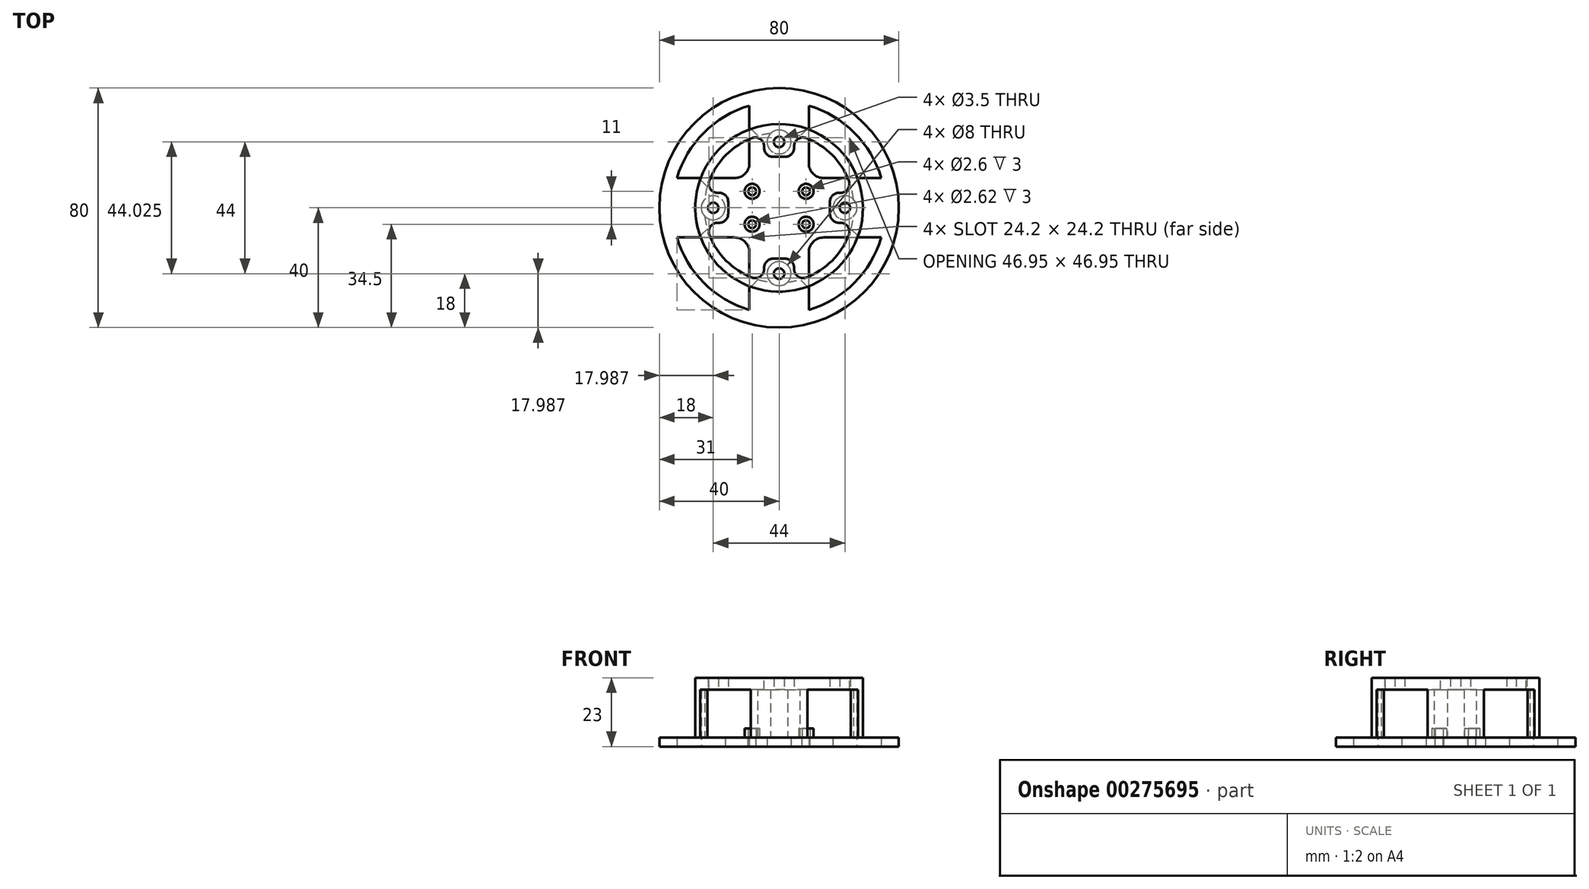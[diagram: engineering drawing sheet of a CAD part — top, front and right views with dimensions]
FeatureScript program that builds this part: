
annotation { "Feature Type Name" : "Feature", "Feature Type Description" : "" }
export const myFeature = defineFeature(function(context is Context, id is Id, definition is map)
    precondition{}
    {
        {
            var Q0;
            Q0=qCreatedBy(makeId("Top.planeOp"),FACE);
            var sketch = newSketch(context, id + "F0", { "sketchPlane" : qUnion([Q0])});
            skCircle(sketch, "E0", {"center": v(0, 0) * mm, "radius": 40 * mm});
            skSolve(sketch);
        }
        {
            var Q0;
            Q0 = qSketchRegion(id + "F0", true);
            extrude(context, id + "F1", {"entities" : qUnion([Q0]), "depth" : 3 * mm});
        }
        {
            var Q0;
            Q0=makeQuery(id+"F1.opExtrude","CAP_FACE",FACE,{"disambiguationData":[OSD([sQuery(id+"F0.wireOp",EDGE,"E0")])],"isStart":false});
            var sketch = newSketch(context, id + "F2", { "sketchPlane" : qUnion([Q0])});
            skPoint(sketch, "E1.center", {"position": v(0, 0) * mm});
            skCircle(sketch, "E2", {"center": v(0, 0) * mm, "radius": 28 * mm});
            skSolve(sketch);
        }
        {
            var Q0;
            Q0 = qSketchRegion(id + "F2", true);
            extrude(context, id + "F3", {"entities" : qUnion([Q0]), "operationType" : NewBodyOperationType.ADD, "depth" : 16 * mm});
        }
        {
            var Q0;
            Q0=makeQuery(id+"F3.opExtrude","CAP_FACE",FACE,{"disambiguationData":[OSD([sQuery(id+"F2.wireOp",EDGE,"E2")])],"isStart":false});
            var sketch = newSketch(context, id + "F4", { "sketchPlane" : qUnion([Q0])});
            skCircle(sketch, "E3", {"center": v(0, 0) * mm, "radius": 25 * mm});
            skSolve(sketch);
        }
        {
            var Q0;
            Q0 = qSketchRegion(id + "F4", true);
            extrude(context, id + "F5", {"entities" : qUnion([Q0]), "operationType" : NewBodyOperationType.REMOVE, "oppositeDirection" : true, "depth" : 16 * mm});
        }
        {
            var Q0;
            Q0=makeQuery(id+"F3.opExtrude","CAP_FACE",FACE,{"disambiguationData":[OSD([sQuery(id+"F2.wireOp",EDGE,"E2")])],"isStart":false});
            var sketch = newSketch(context, id + "F6", { "sketchPlane" : qUnion([Q0])});
            skPoint(sketch, "E4", {"position": v(0, 22) * mm});
            skLineSegment(sketch, "E5.bottom", {"start": v(5, 17) * mm, "end": v(-5, 17) * mm});
            skLineSegment(sketch, "E5.left", {"start": v(5, 17) * mm, "end": v(5, 24.5) * mm});
            skLineSegment(sketch, "E5.right", {"start": v(-5, 17) * mm, "end": v(-5, 24.5) * mm});
            skCircle(sketch, "E6", {"center": v(0, 0) * mm, "radius": 28 * mm});
            skCircle(sketch, "E7", {"center": v(0, 0) * mm, "radius": 25 * mm});
            skCircle(sketch, "E8", {"center": v(0, 22) * mm, "radius": 1.75 * mm});
            skLineSegment(sketch, "E9.1.0", {"start": v(-17, 5) * mm, "end": v(-17, -5) * mm});
            skLineSegment(sketch, "E9.1.1", {"start": v(-17, -5) * mm, "end": v(-24.5, -5) * mm});
            skCircle(sketch, "E9.1.2", {"center": v(-22, 0) * mm, "radius": 1.75 * mm});
            skPoint(sketch, "E9.1.3", {"position": v(-22, 0) * mm});
            skLineSegment(sketch, "E9.1.4", {"start": v(-17, 5) * mm, "end": v(-24.5, 5) * mm});
            skLineSegment(sketch, "E9.2.0", {"start": v(-5, -17) * mm, "end": v(5, -17) * mm});
            skLineSegment(sketch, "E9.2.1", {"start": v(5, -17) * mm, "end": v(5, -24.5) * mm});
            skCircle(sketch, "E9.2.2", {"center": v(0, -22) * mm, "radius": 1.75 * mm});
            skPoint(sketch, "E9.2.3", {"position": v(0, -22) * mm});
            skLineSegment(sketch, "E9.2.4", {"start": v(-5, -17) * mm, "end": v(-5, -24.5) * mm});
            skLineSegment(sketch, "E9.3.0", {"start": v(17, -5) * mm, "end": v(17, 5) * mm});
            skLineSegment(sketch, "E9.3.1", {"start": v(17, 5) * mm, "end": v(24.5, 5) * mm});
            skCircle(sketch, "E9.3.2", {"center": v(22, 0) * mm, "radius": 1.75 * mm});
            skPoint(sketch, "E9.3.3", {"position": v(22, 0) * mm});
            skLineSegment(sketch, "E9.3.4", {"start": v(17, -5) * mm, "end": v(24.5, -5) * mm});
            skPoint(sketch, "E5.top.start.orphan", {"position": v(5, 27) * mm});
            skPoint(sketch, "E10.orphan", {"position": v(-5, 27) * mm});
            skPoint(sketch, "E11.orphan", {"position": v(-27, -5) * mm});
            skPoint(sketch, "E12.orphan", {"position": v(27, -5) * mm});
            skPoint(sketch, "E13.orphan", {"position": v(-5, -27) * mm});
            skSolve(sketch);
        }
        {
            var Q0;
            Q0=makeQuery(id+"F6.imprint","IMPRINT",FACE,{"disambiguationData":[TD([[makeQuery(id+"F6.imprint","IMPRINT",EDGE,{"derivedFrom":sQuery(id+"F6.wireOp",EDGE,"E9.1.0")}),-1.0]])]});
            var Q1;
            Q1=makeQuery(id+"F6.imprint","IMPRINT",FACE,{"disambiguationData":[TD([[makeQuery(id+"F6.imprint","IMPRINT",EDGE,{"derivedFrom":sQuery(id+"F6.wireOp",EDGE,"E5.bottom")}),-1.0]])]});
            var Q2;
            Q2=makeQuery(id+"F6.imprint","IMPRINT",FACE,{"disambiguationData":[TD([[makeQuery(id+"F6.imprint","IMPRINT",EDGE,{"derivedFrom":sQuery(id+"F6.wireOp",EDGE,"E9.3.0")}),-1.0]])]});
            var Q3;
            Q3=makeQuery(id+"F6.imprint","IMPRINT",FACE,{"disambiguationData":[TD([[makeQuery(id+"F6.imprint","IMPRINT",EDGE,{"derivedFrom":sQuery(id+"F6.wireOp",EDGE,"E9.2.0")}),-1.0]])]});
            var Q4;
            Q4=makeQuery(id+"F6.imprint","IMPRINT",FACE,{"disambiguationData":[TD([[makeQuery(id+"F6.imprint","IMPRINT",EDGE,{"derivedFrom":sQuery(id+"F6.wireOp",EDGE,"E6")}),1.0]])]});
            extrude(context, id + "F7", {"entities" : qUnion([Q0, Q1, Q2, Q3, Q4]), "operationType" : NewBodyOperationType.ADD, "depth" : 4 * mm});
        }
        {
            var Q0;
            Q0=makeQuery(id+"F7.opExtrude","SWEPT_EDGE",EDGE,{"disambiguationData":[OSD([sQuery(id+"F6.wireOp",EDGE,"E9.1.0"),sQuery(id+"F6.wireOp",EDGE,"E9.1.1")])]});
            var Q1;
            Q1=makeQuery(id+"F7.opExtrude","SWEPT_EDGE",EDGE,{"disambiguationData":[OSD([sQuery(id+"F6.wireOp",EDGE,"E9.1.0"),sQuery(id+"F6.wireOp",EDGE,"E9.1.4")])]});
            var Q2;
            Q2=makeQuery(id+"F7.opExtrude","SWEPT_EDGE",EDGE,{"disambiguationData":[OSD([sQuery(id+"F6.wireOp",EDGE,"E5.bottom"),sQuery(id+"F6.wireOp",EDGE,"E5.right")])]});
            var Q3;
            Q3=makeQuery(id+"F7.opExtrude","SWEPT_EDGE",EDGE,{"disambiguationData":[OSD([sQuery(id+"F6.wireOp",EDGE,"E5.bottom"),sQuery(id+"F6.wireOp",EDGE,"E5.left")])]});
            var Q4;
            Q4=makeQuery(id+"F7.opExtrude","SWEPT_EDGE",EDGE,{"disambiguationData":[OSD([sQuery(id+"F6.wireOp",EDGE,"E5.left"),sQuery(id+"F6.wireOp",EDGE,"E7")])]});
            var Q5;
            Q5=makeQuery(id+"F7.opExtrude","SWEPT_EDGE",EDGE,{"disambiguationData":[OSD([sQuery(id+"F6.wireOp",EDGE,"E5.right"),sQuery(id+"F6.wireOp",EDGE,"E7")])]});
            var Q6;
            Q6=makeQuery(id+"F7.opExtrude","SWEPT_EDGE",EDGE,{"disambiguationData":[OSD([sQuery(id+"F6.wireOp",EDGE,"E7"),sQuery(id+"F6.wireOp",EDGE,"E9.1.4")])]});
            var Q7;
            Q7=makeQuery(id+"F7.opExtrude","SWEPT_EDGE",EDGE,{"disambiguationData":[OSD([sQuery(id+"F6.wireOp",EDGE,"E7"),sQuery(id+"F6.wireOp",EDGE,"E9.1.1")])]});
            var Q8;
            Q8=makeQuery(id+"F7.opExtrude","SWEPT_EDGE",EDGE,{"disambiguationData":[OSD([sQuery(id+"F6.wireOp",EDGE,"E9.3.0"),sQuery(id+"F6.wireOp",EDGE,"E9.3.4")])]});
            var Q9;
            Q9=makeQuery(id+"F7.opExtrude","SWEPT_EDGE",EDGE,{"disambiguationData":[OSD([sQuery(id+"F6.wireOp",EDGE,"E9.3.0"),sQuery(id+"F6.wireOp",EDGE,"E9.3.1")])]});
            var Q10;
            Q10=makeQuery(id+"F7.opExtrude","SWEPT_EDGE",EDGE,{"disambiguationData":[OSD([sQuery(id+"F6.wireOp",EDGE,"E7"),sQuery(id+"F6.wireOp",EDGE,"E9.3.1")])]});
            var Q11;
            Q11=makeQuery(id+"F7.opExtrude","SWEPT_EDGE",EDGE,{"disambiguationData":[OSD([sQuery(id+"F6.wireOp",EDGE,"E7"),sQuery(id+"F6.wireOp",EDGE,"E9.3.4")])]});
            var Q12;
            Q12=makeQuery(id+"F7.opExtrude","SWEPT_EDGE",EDGE,{"disambiguationData":[OSD([sQuery(id+"F6.wireOp",EDGE,"E9.2.0"),sQuery(id+"F6.wireOp",EDGE,"E9.2.1")])]});
            var Q13;
            Q13=makeQuery(id+"F7.opExtrude","SWEPT_EDGE",EDGE,{"disambiguationData":[OSD([sQuery(id+"F6.wireOp",EDGE,"E9.2.0"),sQuery(id+"F6.wireOp",EDGE,"E9.2.4")])]});
            var Q14;
            Q14=makeQuery(id+"F7.opExtrude","SWEPT_EDGE",EDGE,{"disambiguationData":[OSD([sQuery(id+"F6.wireOp",EDGE,"E7"),sQuery(id+"F6.wireOp",EDGE,"E9.2.4")])]});
            var Q15;
            Q15=makeQuery(id+"F7.opExtrude","SWEPT_EDGE",EDGE,{"disambiguationData":[OSD([sQuery(id+"F6.wireOp",EDGE,"E7"),sQuery(id+"F6.wireOp",EDGE,"E9.2.1")])]});
            fillet(context, id + "F8", {"entities" : qUnion([Q0, Q1, Q2, Q3, Q4, Q5, Q6, Q7, Q8, Q9, Q10, Q11, Q12, Q13, Q14, Q15]), "radius" : 3 * mm, "tangentPropagation" : true, "allowEdgeOverflow" : false});
        }
        {
            var Q0;
            Q0=makeQuery(id+"F1.opExtrude","CAP_FACE",FACE,{"disambiguationData":[OSD([sQuery(id+"F0.wireOp",EDGE,"E0")])],"isStart":true});
            var sketch = newSketch(context, id + "F9", { "sketchPlane" : qUnion([Q0])});
            skCircle(sketch, "E14", {"center": v(0, 22) * mm, "radius": 4 * mm});
            skCircle(sketch, "E15.1.0", {"center": v(-22, 0) * mm, "radius": 4 * mm});
            skCircle(sketch, "E15.2.0", {"center": v(0, -22) * mm, "radius": 4 * mm});
            skCircle(sketch, "E15.3.0", {"center": v(22, 0) * mm, "radius": 4 * mm});
            skPoint(sketch, "E15.center", {"position": v(0, 0) * mm});
            skSolve(sketch);
        }
        {
            var Q0;
            Q0=makeQuery(id+"F9.imprint","IMPRINT",FACE,{"disambiguationData":[TD([[makeQuery(id+"F9.imprint","IMPRINT",EDGE,{"derivedFrom":sQuery(id+"F9.wireOp",EDGE,"E14")}),1.0]])]});
            var Q1;
            Q1=makeQuery(id+"F9.imprint","IMPRINT",FACE,{"disambiguationData":[TD([[makeQuery(id+"F9.imprint","IMPRINT",EDGE,{"derivedFrom":sQuery(id+"F9.wireOp",EDGE,"E15.1.0")}),1.0]])]});
            var Q2;
            Q2=makeQuery(id+"F9.imprint","IMPRINT",FACE,{"disambiguationData":[TD([[makeQuery(id+"F9.imprint","IMPRINT",EDGE,{"derivedFrom":sQuery(id+"F9.wireOp",EDGE,"E15.2.0")}),1.0]])]});
            var Q3;
            Q3=makeQuery(id+"F9.imprint","IMPRINT",FACE,{"disambiguationData":[TD([[makeQuery(id+"F9.imprint","IMPRINT",EDGE,{"derivedFrom":sQuery(id+"F9.wireOp",EDGE,"E15.3.0")}),1.0]])]});
            var Q4;
            {var subQ0=sQuery(id+"F6.wireOp",EDGE,"E9.1.1");var subQ1=sQuery(id+"F6.wireOp",EDGE,"E7");var subQ2=sQuery(id+"F6.wireOp",EDGE,"E9.2.4");var subQ3=sQuery(id+"F6.wireOp",EDGE,"E5.right");var subQ4=sQuery(id+"F6.wireOp",EDGE,"E9.1.4");var subQ5=makeQuery(id+"F7.opExtrude","SWEPT_FACE",FACE,{"disambiguationData":[OSD([subQ0])]});var subQ6=sQuery(id+"F6.wireOp",EDGE,"E5.left");var subQ7=sQuery(id+"F6.wireOp",EDGE,"E9.3.1");var subQ8=sQuery(id+"F6.wireOp",EDGE,"E9.1.0");var subQ9=sQuery(id+"F6.wireOp",EDGE,"E9.2.1");var subQ10=sQuery(id+"F6.wireOp",EDGE,"E9.3.4");var subQ11=sQuery(id+"F6.wireOp",EDGE,"E9.1.2");Q4=makeQuery(id+"F8.opFillet","BLEND_VERTEX",VERTEX,{"blendedFrom":[makeQuery(id+"F7.opExtrude","SWEPT_EDGE",EDGE,{"disambiguationData":[OSD([subQ8,subQ0])]}),subQ5,makeQuery(id+"F7.boolean.opBoolean","SPLIT",FACE,{"disambiguationData":[TD([makeQuery(id+"F7.opExtrude","SWEPT_FACE",FACE,{"disambiguationData":[OSD([subQ8])]})])],"derivedFrom":makeQuery(id+"F7.opExtrude","CAP_FACE",FACE,{"disambiguationData":[OSD([sQuery(id+"F6.wireOp",EDGE,"E5.bottom"),subQ6,subQ3,sQuery(id+"F6.wireOp",EDGE,"E6"),subQ1,sQuery(id+"F6.wireOp",EDGE,"E8"),subQ8,subQ0,subQ11,subQ4,sQuery(id+"F6.wireOp",EDGE,"E9.2.0"),subQ9,sQuery(id+"F6.wireOp",EDGE,"E9.2.2"),subQ2,sQuery(id+"F6.wireOp",EDGE,"E9.3.0"),subQ7,sQuery(id+"F6.wireOp",EDGE,"E9.3.2"),subQ10])],"isStart":true})})],"blendedInto":[subQ5,makeQuery(id+"F7.boolean.opBoolean","SPLIT",FACE,{"disambiguationData":[TD([makeQuery(id+"F7.opExtrude","SWEPT_FACE",FACE,{"disambiguationData":[OSD([subQ8])]})])],"derivedFrom":makeQuery(id+"F7.opExtrude","CAP_FACE",FACE,{"disambiguationData":[OSD([sQuery(id+"F6.wireOp",EDGE,"E5.bottom"),subQ6,subQ3,sQuery(id+"F6.wireOp",EDGE,"E6"),subQ1,sQuery(id+"F6.wireOp",EDGE,"E8"),subQ8,subQ0,subQ11,subQ4,sQuery(id+"F6.wireOp",EDGE,"E9.2.0"),subQ9,sQuery(id+"F6.wireOp",EDGE,"E9.2.2"),subQ2,sQuery(id+"F6.wireOp",EDGE,"E9.3.0"),subQ7,sQuery(id+"F6.wireOp",EDGE,"E9.3.2"),subQ10])],"isStart":true})})]});}
            extrude(context, id + "F10", {"entities" : qUnion([Q0, Q1, Q2, Q3]), "operationType" : NewBodyOperationType.REMOVE, "endBound" : BoundingType.UP_TO_VERTEX, "oppositeDirection" : true, "endBoundEntityVertex" : qUnion([Q4]), "depth" : 25 * mm});
        }
        {
            var Q0;
            Q0=makeQuery(id+"F7.opExtrude","CAP_FACE",FACE,{"disambiguationData":[OSD([sQuery(id+"F6.wireOp",EDGE,"E5.bottom"),sQuery(id+"F6.wireOp",EDGE,"E5.left"),sQuery(id+"F6.wireOp",EDGE,"E5.right"),sQuery(id+"F6.wireOp",EDGE,"E6"),sQuery(id+"F6.wireOp",EDGE,"E7"),sQuery(id+"F6.wireOp",EDGE,"E8"),sQuery(id+"F6.wireOp",EDGE,"E9.1.0"),sQuery(id+"F6.wireOp",EDGE,"E9.1.1"),sQuery(id+"F6.wireOp",EDGE,"E9.1.2"),sQuery(id+"F6.wireOp",EDGE,"E9.1.4"),sQuery(id+"F6.wireOp",EDGE,"E9.2.0"),sQuery(id+"F6.wireOp",EDGE,"E9.2.1"),sQuery(id+"F6.wireOp",EDGE,"E9.2.2"),sQuery(id+"F6.wireOp",EDGE,"E9.2.4"),sQuery(id+"F6.wireOp",EDGE,"E9.3.0"),sQuery(id+"F6.wireOp",EDGE,"E9.3.1"),sQuery(id+"F6.wireOp",EDGE,"E9.3.2"),sQuery(id+"F6.wireOp",EDGE,"E9.3.4")])],"isStart":false});
            var sketch = newSketch(context, id + "F11", { "sketchPlane" : qUnion([Q0])});
            skLineSegment(sketch, "E16", {"start": v(0, 0) * mm, "end": v(-19.8, -19.8) * mm, "construction": true});
            skLineSegment(sketch, "E17", {"start": v(0, 0) * mm, "end": v(-19.8, 19.8) * mm, "construction": true});
            skSolve(sketch);
        }
        {
            var Q0;
            Q0=sQuery(id+"F11.wireOp",EDGE,"E16");
            var Q1;
            Q1=sQuery(id+"F11.wireOp",VERTEX,"E16.end");
            cPlane(context, id + "F12", {"entities" : qUnion([Q0, Q1]), "cplaneType" : CPlaneType.LINE_POINT, "offset" : 25 * mm, "width" : 150 * mm, "height" : 150 * mm});
        }
        {
            var Q0;
            Q0=qCreatedBy(id+"F12.planeOp",FACE);
            var sketch = newSketch(context, id + "F13", { "sketchPlane" : qUnion([Q0])});
            skLineSegment(sketch, "E18.bottom", {"start": v(-12, 19) * mm, "end": v(12, 19) * mm});
            skLineSegment(sketch, "E18.top", {"start": v(-12, 3) * mm, "end": v(12, 3) * mm});
            skLineSegment(sketch, "E18.left", {"start": v(-12, 19) * mm, "end": v(-12, 3) * mm});
            skLineSegment(sketch, "E18.right", {"start": v(12, 19) * mm, "end": v(12, 3) * mm});
            skSolve(sketch);
        }
        {
            var Q0;
            Q0 = qSketchRegion(id + "F13", true);
            extrude(context, id + "F14", {"entities" : qUnion([Q0]), "operationType" : NewBodyOperationType.REMOVE, "endBound" : BoundingType.THROUGH_ALL, "oppositeDirection" : true, "depth" : 25 * mm});
        }
        {
            var Q0;
            Q0=sQuery(id+"F11.wireOp",VERTEX,"E17.end");
            var Q1;
            Q1=sQuery(id+"F11.wireOp",EDGE,"E17");
            cPlane(context, id + "F15", {"entities" : qUnion([Q0, Q1]), "cplaneType" : CPlaneType.LINE_POINT, "offset" : 25 * mm, "width" : 150 * mm, "height" : 150 * mm});
        }
        {
            var Q0;
            Q0=qCreatedBy(id+"F15.planeOp",FACE);
            var sketch = newSketch(context, id + "F16", { "sketchPlane" : qUnion([Q0])});
            skLineSegment(sketch, "E19.bottom", {"start": v(-12, 19) * mm, "end": v(12, 19) * mm});
            skLineSegment(sketch, "E19.top", {"start": v(-12, 3) * mm, "end": v(12, 3) * mm});
            skLineSegment(sketch, "E19.left", {"start": v(-12, 19) * mm, "end": v(-12, 3) * mm});
            skLineSegment(sketch, "E19.right", {"start": v(12, 19) * mm, "end": v(12, 3) * mm});
            skSolve(sketch);
        }
        {
            var Q0;
            Q0 = qSketchRegion(id + "F16", true);
            extrude(context, id + "F17", {"entities" : qUnion([Q0]), "operationType" : NewBodyOperationType.REMOVE, "endBound" : BoundingType.THROUGH_ALL, "oppositeDirection" : true, "depth" : 25 * mm});
        }
        {
            var Q0;
            Q0=makeQuery(id+"F5.boolean.opBoolean","COPY",FACE,{"derivedFrom":makeQuery(id+"F5.opExtrude","CAP_FACE",FACE,{"disambiguationData":[OSD([sQuery(id+"F4.wireOp",EDGE,"E3")])],"isStart":false})});
            var sketch = newSketch(context, id + "F18", { "sketchPlane" : qUnion([Q0])});
            skLineSegment(sketch, "E20.bottom", {"start": v(9, -5.5) * mm, "end": v(-9, -5.5) * mm, "construction": true});
            skLineSegment(sketch, "E20.top", {"start": v(9, 5.5) * mm, "end": v(-9, 5.5) * mm, "construction": true});
            skLineSegment(sketch, "E20.left", {"start": v(9, -5.5) * mm, "end": v(9, 5.5) * mm, "construction": true});
            skLineSegment(sketch, "E20.right", {"start": v(-9, -5.5) * mm, "end": v(-9, 5.5) * mm, "construction": true});
            skPoint(sketch, "E20.middle", {"position": v(0, 0) * mm});
            skCircle(sketch, "E21", {"center": v(-9, 5.5) * mm, "radius": 1.3 * mm});
            skCircle(sketch, "E22", {"center": v(9, 5.5) * mm, "radius": 1.3 * mm});
            skCircle(sketch, "E23", {"center": v(9, -5.5) * mm, "radius": 1.3 * mm});
            skCircle(sketch, "E24", {"center": v(-9, -5.5) * mm, "radius": 1.3 * mm});
            skSolve(sketch);
        }
        {
            var Q0;
            Q0 = qSketchRegion(id + "F18", true);
            extrude(context, id + "F19", {"entities" : qUnion([Q0]), "operationType" : NewBodyOperationType.REMOVE, "endBound" : BoundingType.THROUGH_ALL, "oppositeDirection" : true, "depth" : 25 * mm});
        }
        {
            var Q0;
            Q0=makeQuery(id+"F5.boolean.opBoolean","COPY",FACE,{"derivedFrom":makeQuery(id+"F5.opExtrude","CAP_FACE",FACE,{"disambiguationData":[OSD([sQuery(id+"F4.wireOp",EDGE,"E3")])],"isStart":false})});
            var sketch = newSketch(context, id + "F20", { "sketchPlane" : qUnion([Q0])});
            skCircle(sketch, "E25", {"center": v(-9, 5.5) * mm, "radius": 2.5 * mm});
            skCircle(sketch, "E26", {"center": v(-9, 5.5) * mm, "radius": 1.3 * mm});
            skCircle(sketch, "E27", {"center": v(9, 5.5) * mm, "radius": 2.5 * mm});
            skCircle(sketch, "E28", {"center": v(9, 5.5) * mm, "radius": 1.3 * mm});
            skCircle(sketch, "E29", {"center": v(-9, -5.5) * mm, "radius": 2.5 * mm});
            skCircle(sketch, "E30", {"center": v(-9, -5.5) * mm, "radius": 1.3 * mm});
            skCircle(sketch, "E31", {"center": v(9, -5.5) * mm, "radius": 2.5 * mm});
            skCircle(sketch, "E32", {"center": v(9, -5.5) * mm, "radius": 1.3 * mm});
            skSolve(sketch);
        }
        {
            var Q0;
            Q0 = qSketchRegion(id + "F20", true);
            extrude(context, id + "F21", {"entities" : qUnion([Q0]), "operationType" : NewBodyOperationType.ADD, "depth" : 3 * mm});
        }
        {
            var Q0;
            Q0=makeQuery(id+"F1.opExtrude","CAP_FACE",FACE,{"disambiguationData":[OSD([sQuery(id+"F0.wireOp",EDGE,"E0")])],"isStart":true});
            var sketch = newSketch(context, id + "F22", { "sketchPlane" : qUnion([Q0])});
            skCircle(sketch, "E33", {"center": v(0, 0) * mm, "radius": 35.52 * mm});
            skLineSegment(sketch, "E34", {"start": v(-34.11, 9.91) * mm, "end": v(-9.91, 9.91) * mm});
            skLineSegment(sketch, "E35", {"start": v(-9.91, 9.91) * mm, "end": v(-9.91, 34.11) * mm});
            skLineSegment(sketch, "E36", {"start": v(0, 0) * mm, "end": v(-25.12, 25.12) * mm});
            skLineSegment(sketch, "E37.1.0", {"start": v(-9.91, -9.91) * mm, "end": v(-34.11, -9.91) * mm});
            skLineSegment(sketch, "E37.1.1", {"start": v(-9.91, -34.11) * mm, "end": v(-9.91, -9.91) * mm});
            skLineSegment(sketch, "E37.2.0", {"start": v(9.91, -9.91) * mm, "end": v(9.91, -34.11) * mm});
            skLineSegment(sketch, "E37.2.1", {"start": v(34.11, -9.91) * mm, "end": v(9.91, -9.91) * mm});
            skLineSegment(sketch, "E37.3.0", {"start": v(9.91, 9.91) * mm, "end": v(34.11, 9.91) * mm});
            skLineSegment(sketch, "E37.3.1", {"start": v(9.91, 34.11) * mm, "end": v(9.91, 9.91) * mm});
            skSolve(sketch);
        }
        {
            var Q0;
            {var subQ0=sQuery(id+"F22.wireOp",EDGE,"E35");Q0=makeQuery(id+"F22.imprint","IMPRINT",FACE,{"disambiguationData":[TD([[makeQuery(id+"F22.imprint","IMPRINT",EDGE,{"derivedFrom":subQ0}),1.0]])]});}
            var Q1;
            {var subQ0=sQuery(id+"F22.wireOp",EDGE,"E34");Q1=makeQuery(id+"F22.imprint","IMPRINT",FACE,{"disambiguationData":[TD([[makeQuery(id+"F22.imprint","IMPRINT",EDGE,{"derivedFrom":subQ0}),1.0]])]});}
            var Q2;
            {var subQ0=sQuery(id+"F22.wireOp",EDGE,"E37.3.0");Q2=makeQuery(id+"F22.imprint","IMPRINT",FACE,{"disambiguationData":[TD([[makeQuery(id+"F22.imprint","IMPRINT",EDGE,{"derivedFrom":subQ0}),1.0]])]});}
            var Q3;
            {var subQ0=sQuery(id+"F22.wireOp",EDGE,"E37.2.0");Q3=makeQuery(id+"F22.imprint","IMPRINT",FACE,{"disambiguationData":[TD([[makeQuery(id+"F22.imprint","IMPRINT",EDGE,{"derivedFrom":subQ0}),1.0]])]});}
            var Q4;
            {var subQ0=sQuery(id+"F22.wireOp",EDGE,"E37.1.0");Q4=makeQuery(id+"F22.imprint","IMPRINT",FACE,{"disambiguationData":[TD([[makeQuery(id+"F22.imprint","IMPRINT",EDGE,{"derivedFrom":subQ0}),1.0]])]});}
            var Q5;
            {var subQ17=sQuery(id+"F0.wireOp",EDGE,"E0");var subQ18=makeQuery(id+"F1.opExtrude","CAP_FACE",FACE,{"disambiguationData":[OSD([subQ17])],"isStart":false});var subQ19=sQuery(id+"F4.wireOp",EDGE,"E3");var subQ22=makeQuery(id+"F5.boolean.opBoolean","COPY",FACE,{"derivedFrom":makeQuery(id+"F5.opExtrude","CAP_FACE",FACE,{"disambiguationData":[OSD([subQ19])],"isStart":false})});var subQ29=makeQuery(id+"F14.opExtrude","SWEPT_FACE",FACE,{"disambiguationData":[OSD([sQuery(id+"F13.wireOp",EDGE,"E18.top")])]});Q5=makeQuery(id+"F21.boolean.opBoolean","SPLIT",FACE,{"disambiguationData":[TD([makeQuery(id+"F1.opExtrude","SWEPT_FACE",FACE,{"disambiguationData":[OSD([subQ17])]})])],"derivedFrom":makeQuery(id+"F17.boolean.opBoolean","MERGE",FACE,{"derivedFrom":[makeQuery(id+"F14.boolean.opBoolean","MERGE",FACE,{"derivedFrom":[subQ18,subQ22,subQ29]}),makeQuery(id+"F17.opExtrude","SWEPT_FACE",FACE,{"disambiguationData":[OSD([sQuery(id+"F16.wireOp",EDGE,"E19.top")])]})]})});}
            extrude(context, id + "F23", {"entities" : qUnion([Q0, Q1, Q2, Q3, Q4]), "operationType" : NewBodyOperationType.REMOVE, "endBound" : BoundingType.UP_TO_SURFACE, "oppositeDirection" : true, "endBoundEntityFace" : qUnion([Q5]), "depth" : 25 * mm});
        }
        {
            var Q0;
            Q0=makeQuery(id+"F23.boolean.opBoolean","COPY",EDGE,{"derivedFrom":makeQuery(id+"F23.opExtrude","SWEPT_EDGE",EDGE,{"disambiguationData":[OSD([sQuery(id+"F22.wireOp",EDGE,"E37.2.0"),sQuery(id+"F22.wireOp",EDGE,"E37.2.1")])]})});
            var Q1;
            Q1=makeQuery(id+"F23.boolean.opBoolean","COPY",EDGE,{"derivedFrom":makeQuery(id+"F23.opExtrude","SWEPT_EDGE",EDGE,{"disambiguationData":[OSD([sQuery(id+"F22.wireOp",EDGE,"E37.3.0"),sQuery(id+"F22.wireOp",EDGE,"E37.3.1")])]})});
            var Q2;
            Q2=makeQuery(id+"F23.boolean.opBoolean","COPY",EDGE,{"derivedFrom":makeQuery(id+"F23.opExtrude","SWEPT_EDGE",EDGE,{"disambiguationData":[OSD([sQuery(id+"F22.wireOp",EDGE,"E37.1.0"),sQuery(id+"F22.wireOp",EDGE,"E37.1.1")])]})});
            var Q3;
            Q3=makeQuery(id+"F23.boolean.opBoolean","COPY",EDGE,{"derivedFrom":makeQuery(id+"F23.opExtrude","SWEPT_EDGE",EDGE,{"disambiguationData":[OSD([sQuery(id+"F22.wireOp",EDGE,"E34"),sQuery(id+"F22.wireOp",EDGE,"E35"),sQuery(id+"F22.wireOp",EDGE,"E36")])]})});
            fillet(context, id + "F24", {"entities" : qUnion([Q0, Q1, Q2, Q3]), "radius" : 5 * mm, "tangentPropagation" : true, "allowEdgeOverflow" : false});
        }
    });
